# Revit family: efg-20_40ksb2-c_w_60Hz
name_source: partatom
category: 機械設備
units: mm (PartAtom-declared; Revit-internal decimal feet)

## family parameters
OmniClass タイトル = Industrial Ventilating Equipment
OmniClass 番号 = 23.75.35.21.17
パーツ タイプ = 標準
ロード時にボイドで切り取り = はい
丸型コネクタ寸法 = 直径を使用
作業面ベース = いいえ
共有 = いいえ
常に垂直 = はい
部屋計算ポイント = はい

## types (8) — shared parameters
IfcExportAs = IfcFanType
IfcExportType = TUBEAXIAL
MID風量 = 0.0 m³/h
OmniClassCode = 23-33 31 19 11 17
URL = https://www.mitsubishielectric.co.jp
Uniclass2015Code = Pr_65_67_29_67
Uniclass2015Title = Propeller fans
Uniclass2015Version = Systems v1.9
ファンの種類 = 軸流羽根
仕様書バージョン = Version1.0
企業コード = 108420
分類コード = 50052503100110
周波数 = 60 Hz
呼称 = 有圧扇
極 = 4
極数 = 2
法定耐用年数 = 15
相 = 1
製品リリース年月 = 2022年6月1日
製品出荷対象 = 国内
製造元 = 三菱電機株式会社
設置方法 = 壁付
説明 = 業務用有圧換気扇 店舗用 格子タイプ
負荷分類 = 3_ファン類
運転質量 = 0.00 kg
電圧 = 100 V

## per-type parameters (varying)
| type | D1 | Depth | H1 | Height | MAX風量 | MIN風量 | W1 | Width | 価格 | 消費電力 | 羽根径 | 製品質量 | 質量 | 電動機出力 |
| EFG-20KSB2-W | 155  [stored 0.50853 ft] | 235  [stored 0.770997 ft] | 244 | 322  [stored 1.05643 ft] | 640.0 m³/h | 490.0 m³/h | 244 | 322  [stored 1.05643 ft] | 63800 $ | 20 W | ∅200 | 5.30 kg | 6.36 kg | 15 W |
| EFG-20KSB2-C | 155  [stored 0.50853 ft] | 235  [stored 0.770997 ft] | 244 | 322  [stored 1.05643 ft] | 640.0 m³/h | 490.0 m³/h | 244 | 322  [stored 1.05643 ft] | 63800 $ | 20 W | ∅200 | 5.30 kg | 6.36 kg | 15 W |
| EFG-25KSB2-W | 155  [stored 0.50853 ft] | 245 | 294 | 372 | 1210.0 m³/h | 950.0 m³/h | 294 | 372 | 68600 $ | 40 W | ∅250 | 5.60 kg | 6.72 kg | 25 W |
| EFG-25KSB2-C | 155  [stored 0.50853 ft] | 245 | 294 | 372 | 1210.0 m³/h | 950.0 m³/h | 294 | 372 | 68600 $ | 40 W | ∅250 | 5.60 kg | 6.72 kg | 25 W |
| EFG-30KSB2-W | 155  [stored 0.50853 ft] | 265 | 344 | 422 | 1860.0 m³/h | 1310.0 m³/h | 344 | 422 | 83500 $ | 60 W | ∅300 | 7.00 kg | 8.40 kg | 50 W |
| EFG-30KSB2-C | 155  [stored 0.50853 ft] | 265 | 344 | 422 | 1860.0 m³/h | 1310.0 m³/h | 344 | 422 | 83500 $ | 60 W | ∅300 | 7.00 kg | 8.40 kg | 50 W |
| EFG-35KSB2-W | 155  [stored 0.50853 ft] | 275 | 399 | 484 | 2530.0 m³/h | 1950.0 m³/h | 399 | 484 | 121000 $ | 108 W | ∅350 | 10.60 kg | 12.72 kg | 100 W |
| EFG-40KSB2-W | 159 | 341 | 423 | 520 | 3500.0 m³/h | 2700.0 m³/h | 423 | 520 | 156000 $ | 175 W | ∅400 | 17.10 kg | 20.52 kg | 150 W |

note: column(s) folded — value = type name in every type: モデル

note: [stored X ft] marks values corroborated as IEEE doubles in the binary element streams (Revit-internal decimal feet)
